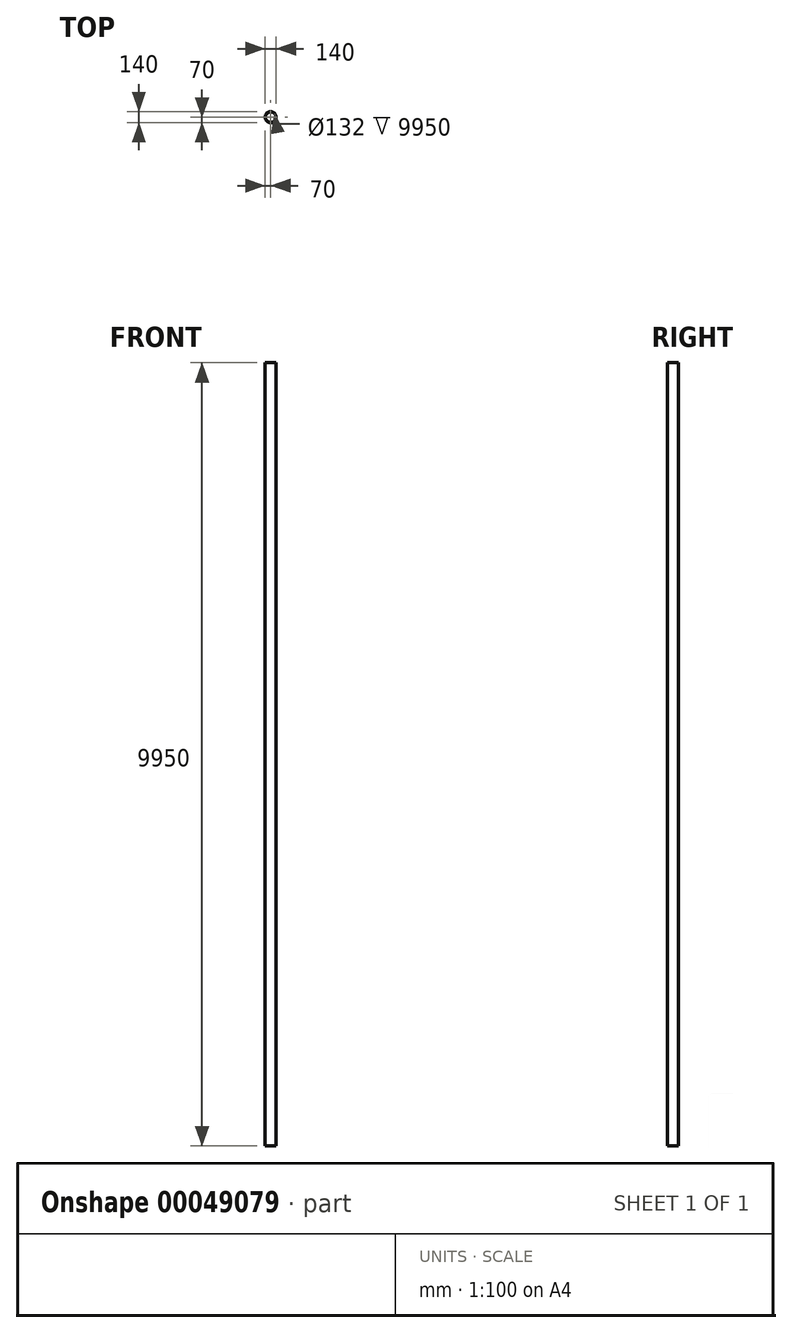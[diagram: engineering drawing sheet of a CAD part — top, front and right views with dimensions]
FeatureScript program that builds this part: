
annotation { "Feature Type Name" : "Feature", "Feature Type Description" : "" }
export const myFeature = defineFeature(function(context is Context, id is Id, definition is map)
    precondition{}
    {
        {
            var Q0;
            Q0=qCreatedBy(makeId("Top.planeOp"),FACE);
            var sketch = newSketch(context, id + "F0", { "sketchPlane" : qUnion([Q0])});
            skCircle(sketch, "E0", {"center": v(0, 0) * mm, "radius": 70 * mm});
            skCircle(sketch, "E1", {"center": v(0, 0) * mm, "radius": 66 * mm});
            skSolve(sketch);
        }
        {
            var Q0;
            Q0=makeQuery(id+"F0.imprint","IMPRINT",FACE,{"disambiguationData":[TD([[makeQuery(id+"F0.imprint","IMPRINT",EDGE,{"derivedFrom":sQuery(id+"F0.wireOp",EDGE,"E0")}),1.0]])]});
            extrude(context, id + "F1", {"entities" : qUnion([Q0]), "depth" : 9950 * mm});
        }
    });
